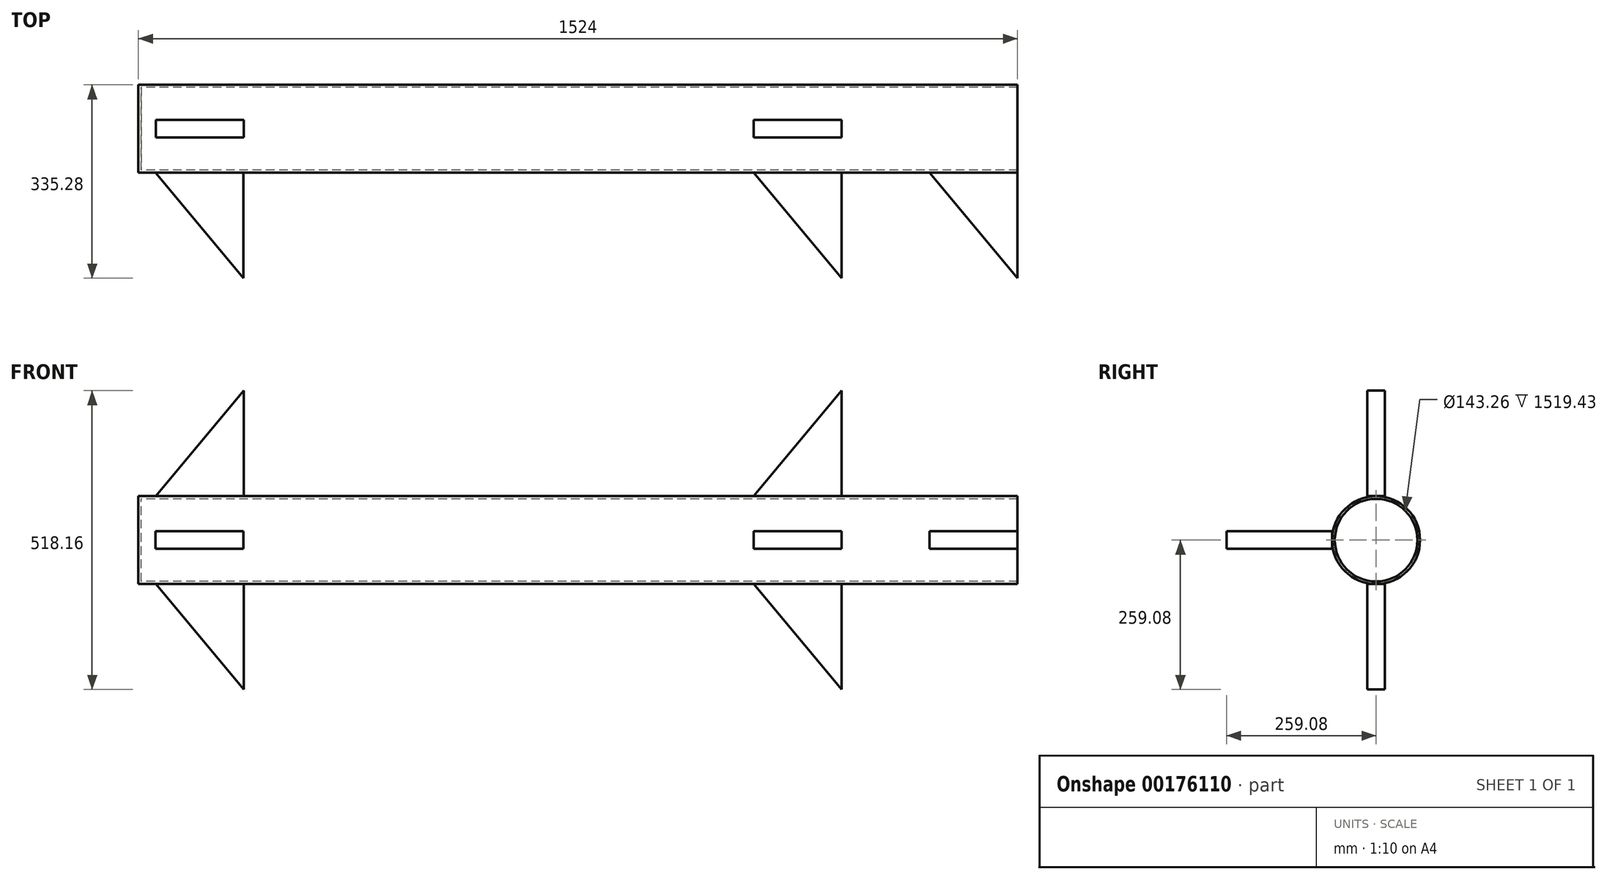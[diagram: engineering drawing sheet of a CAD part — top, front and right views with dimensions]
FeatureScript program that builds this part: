
annotation { "Feature Type Name" : "Feature", "Feature Type Description" : "" }
export const myFeature = defineFeature(function(context is Context, id is Id, definition is map)
    precondition{}
    {
        {
            var Q0;
            Q0=qCreatedBy(makeId("Top.planeOp"),FACE);
            var sketch = newSketch(context, id + "F0", { "sketchPlane" : qUnion([Q0])});
            skLineSegment(sketch, "E0.bottom", {"start": v(762, -76.2) * mm, "end": v(-762, -76.2) * mm});
            skLineSegment(sketch, "E0.top", {"start": v(762, 76.2) * mm, "end": v(-762, 76.2) * mm});
            skLineSegment(sketch, "E0.left", {"start": v(762, -76.2) * mm, "end": v(762, 76.2) * mm});
            skPoint(sketch, "E0.middle", {"position": v(0, 0) * mm});
            skLineSegment(sketch, "E1", {"start": v(-1020.66, 0) * mm, "end": v(-762, -76.2) * mm});
            skLineSegment(sketch, "E2", {"start": v(609.6, 76.2) * mm, "end": v(762, 76.2) * mm});
            skLineSegment(sketch, "E3", {"start": v(762, 76.2) * mm, "end": v(762, 259.08) * mm});
            skLineSegment(sketch, "E4", {"start": v(609.6, 76.2) * mm, "end": v(762, 259.08) * mm});
            skLineSegment(sketch, "E5", {"start": v(762, -76.2) * mm, "end": v(762, -259.08) * mm});
            skLineSegment(sketch, "E6", {"start": v(609.6, -76.2) * mm, "end": v(762, -259.08) * mm});
            skLineSegment(sketch, "E7", {"start": v(-762, 76.2) * mm, "end": v(-732.22, 76.2) * mm});
            skLineSegment(sketch, "E8", {"start": v(-732.22, 76.2) * mm, "end": v(-579.82, 76.2) * mm});
            skLineSegment(sketch, "E9", {"start": v(-579.82, 76.2) * mm, "end": v(-579.82, 259.08) * mm});
            skLineSegment(sketch, "E10", {"start": v(-732.22, 76.2) * mm, "end": v(-579.82, 259.08) * mm});
            skLineSegment(sketch, "E11", {"start": v(-579.82, -76.2) * mm, "end": v(-579.82, -259.08) * mm});
            skLineSegment(sketch, "E12", {"start": v(-732.22, -76.2) * mm, "end": v(-579.82, -259.08) * mm});
            skPoint(sketch, "E13.endSnap0", {"position": v(762, 0) * mm});
            skLineSegment(sketch, "E14", {"start": v(457.2, 76.2) * mm, "end": v(457.2, -76.2) * mm});
            skLineSegment(sketch, "E15", {"start": v(457.2, 76.2) * mm, "end": v(304.8, 76.2) * mm});
            skLineSegment(sketch, "E16", {"start": v(457.2, 76.2) * mm, "end": v(457.2, 259.08) * mm});
            skLineSegment(sketch, "E17", {"start": v(457.2, 0) * mm, "end": v(762, 0) * mm});
            skLineSegment(sketch, "E18", {"start": v(304.8, 76.2) * mm, "end": v(457.2, 259.08) * mm});
            skLineSegment(sketch, "E19", {"start": v(457.2, -76.2) * mm, "end": v(457.2, -259.08) * mm});
            skLineSegment(sketch, "E20", {"start": v(304.8, -76.2) * mm, "end": v(457.2, -259.08) * mm});
            skLineSegment(sketch, "E21", {"start": v(0, 0) * mm, "end": v(-761.8, 0) * mm});
            skLineSegment(sketch, "E22", {"start": v(0, 0) * mm, "end": v(762, 0) * mm});
            skLineSegment(sketch, "E23", {"start": v(-761.8, 0) * mm, "end": v(-1020.66, 0) * mm, "construction": true});
            skLineSegment(sketch, "E24", {"start": v(-761.8, 0) * mm, "end": v(-762, -76.2) * mm});
            skLineSegment(sketch, "E25", {"start": v(-761.8, 0) * mm, "end": v(-762, 76.2) * mm});
            skLineSegment(sketch, "E26", {"start": v(304.8, 76.2) * mm, "end": v(0, 76.2) * mm});
            skSolve(sketch);
        }
        {
            var Q0;
            Q0=qCreatedBy(makeId("Right.planeOp"),FACE);
            var sketch = newSketch(context, id + "F1", { "sketchPlane" : qUnion([Q0])});
            skCircle(sketch, "E27", {"center": v(0, 0) * mm, "radius": 76.2 * mm});
            skSolve(sketch);
        }
        {
            var Q0;
            Q0=makeQuery(id+"F1.imprint","IMPRINT",FACE,{"disambiguationData":[TD([[makeQuery(id+"F1.imprint","IMPRINT",EDGE,{"derivedFrom":sQuery(id+"F1.wireOp",EDGE,"E27")}),1.0]])]});
            extrude(context, id + "F2", {"entities" : qUnion([Q0]), "depth" : 762 * mm, "hasSecondDirection" : true, "secondDirectionOppositeDirection" : true, "secondDirectionDepth" : 762 * mm});
        }
        {
            var Q0;
            Q0=sQuery(id+"F0.wireOp",EDGE,"E24");
            var Q1;
            Q1=sQuery(id+"F0.wireOp",EDGE,"E1");
            var Q2;
            Q2=sQuery(id+"F0.wireOp",EDGE,"E23");
            revolve(context, id + "F3", {"bodyType" : ToolBodyType.SURFACE, "surfaceEntities" : qUnion([Q0, Q1]), "axis" : qUnion([Q2]), "revolveType" : RevolveType.FULL});
        }
        {
            var Q0;
            Q0=makeQuery(id+"F0.imprint","IMPRINT",FACE,{"disambiguationData":[TD([[makeQuery(id+"F0.imprint","IMPRINT",EDGE,{"derivedFrom":sQuery(id+"F0.wireOp",EDGE,"E8")}),1.0]])]});
            var Q1;
            {var subQ0=sQuery(id+"F0.wireOp",EDGE,"E11");Q1=makeQuery(id+"F0.imprint","IMPRINT",FACE,{"disambiguationData":[TD([[makeQuery(id+"F0.imprint","IMPRINT",EDGE,{"derivedFrom":subQ0}),-1.0]])]});}
            var Q2;
            {var subQ0=sQuery(id+"F0.wireOp",EDGE,"E19");Q2=makeQuery(id+"F0.imprint","IMPRINT",FACE,{"disambiguationData":[TD([[makeQuery(id+"F0.imprint","IMPRINT",EDGE,{"derivedFrom":subQ0}),-1.0]])]});}
            var Q3;
            Q3=makeQuery(id+"F0.imprint","IMPRINT",FACE,{"disambiguationData":[TD([[makeQuery(id+"F0.imprint","IMPRINT",EDGE,{"derivedFrom":sQuery(id+"F0.wireOp",EDGE,"E15")}),-1.0]])]});
            var Q4;
            Q4=makeQuery(id+"F0.imprint","IMPRINT",FACE,{"disambiguationData":[TD([[makeQuery(id+"F0.imprint","IMPRINT",EDGE,{"derivedFrom":sQuery(id+"F0.wireOp",EDGE,"E2")}),1.0]])]});
            var Q5;
            {var subQ0=sQuery(id+"F0.wireOp",EDGE,"E5");Q5=makeQuery(id+"F0.imprint","IMPRINT",FACE,{"disambiguationData":[TD([[makeQuery(id+"F0.imprint","IMPRINT",EDGE,{"derivedFrom":subQ0}),-1.0]])]});}
            extrude(context, id + "F4", {"entities" : qUnion([Q0, Q1, Q2, Q3, Q4, Q5]), "operationType" : NewBodyOperationType.ADD, "depth" : 15.24 * mm, "hasSecondDirection" : true, "secondDirectionOppositeDirection" : true, "secondDirectionDepth" : 15.24 * mm});
        }
        {
            var Q0;
            Q0=qCreatedBy(makeId("Front.planeOp"),FACE);
            var sketch = newSketch(context, id + "F5", { "sketchPlane" : qUnion([Q0])});
            skLineSegment(sketch, "E28", {"start": v(0, 0) * mm, "end": v(0, -76.2) * mm});
            skLineSegment(sketch, "E29", {"start": v(0, -76.2) * mm, "end": v(304.8, -76.2) * mm});
            skLineSegment(sketch, "E30", {"start": v(304.8, -76.2) * mm, "end": v(457.2, -76.2) * mm});
            skLineSegment(sketch, "E31", {"start": v(457.2, -76.2) * mm, "end": v(457.2, -259.08) * mm});
            skLineSegment(sketch, "E32", {"start": v(457.2, -259.08) * mm, "end": v(304.8, -76.2) * mm});
            skLineSegment(sketch, "E33", {"start": v(457.2, -76.2) * mm, "end": v(762, -76.2) * mm});
            skLineSegment(sketch, "E34", {"start": v(762, -76.2) * mm, "end": v(609.6, -76.2) * mm});
            skLineSegment(sketch, "E35", {"start": v(762, -76.2) * mm, "end": v(762, -259.08) * mm});
            skLineSegment(sketch, "E36", {"start": v(762, -259.08) * mm, "end": v(609.6, -76.2) * mm});
            skLineSegment(sketch, "E37", {"start": v(0, 0) * mm, "end": v(914.4, 0) * mm, "construction": true});
            skLineSegment(sketch, "E38", {"start": v(0, 0) * mm, "end": v(0, 76.2) * mm});
            skLineSegment(sketch, "E39", {"start": v(0, 76.2) * mm, "end": v(304.8, 76.2) * mm});
            skLineSegment(sketch, "E40", {"start": v(304.8, 76.2) * mm, "end": v(457.2, 76.2) * mm});
            skLineSegment(sketch, "E41", {"start": v(457.2, 76.2) * mm, "end": v(457.2, 259.08) * mm});
            skLineSegment(sketch, "E42", {"start": v(304.8, 76.2) * mm, "end": v(457.2, 259.08) * mm});
            skLineSegment(sketch, "E43", {"start": v(457.2, 76.2) * mm, "end": v(762, 76.2) * mm});
            skLineSegment(sketch, "E44", {"start": v(762, 76.2) * mm, "end": v(609.6, 76.2) * mm});
            skLineSegment(sketch, "E45", {"start": v(762, 76.2) * mm, "end": v(762, 259.08) * mm});
            skLineSegment(sketch, "E46", {"start": v(762, 259.08) * mm, "end": v(609.6, 76.2) * mm});
            skLineSegment(sketch, "E47", {"start": v(0, -76.2) * mm, "end": v(-579.12, -76.2) * mm});
            skLineSegment(sketch, "E48", {"start": v(-579.12, -76.2) * mm, "end": v(-731.52, -76.2) * mm});
            skLineSegment(sketch, "E49", {"start": v(-579.12, -76.2) * mm, "end": v(-579.12, -259.08) * mm});
            skLineSegment(sketch, "E50", {"start": v(-579.12, -259.08) * mm, "end": v(-731.52, -76.2) * mm});
            skLineSegment(sketch, "E51", {"start": v(0, 76.2) * mm, "end": v(-579.12, 76.2) * mm});
            skLineSegment(sketch, "E52", {"start": v(-579.12, 76.2) * mm, "end": v(-579.12, 259.08) * mm});
            skLineSegment(sketch, "E53", {"start": v(-579.12, 76.2) * mm, "end": v(-731.52, 76.2) * mm});
            skLineSegment(sketch, "E54", {"start": v(-731.52, 76.2) * mm, "end": v(-579.12, 259.08) * mm});
            skSolve(sketch);
        }
        {
            var Q0;
            Q0=makeQuery(id+"F5.imprint","IMPRINT",FACE,{"disambiguationData":[TD([[makeQuery(id+"F5.imprint","IMPRINT",EDGE,{"derivedFrom":sQuery(id+"F5.wireOp",EDGE,"E34")}),1.0]])]});
            var Q1;
            Q1=makeQuery(id+"F5.imprint","IMPRINT",FACE,{"disambiguationData":[TD([[makeQuery(id+"F5.imprint","IMPRINT",EDGE,{"derivedFrom":sQuery(id+"F5.wireOp",EDGE,"E44")}),-1.0]])]});
            var Q2;
            Q2=makeQuery(id+"F5.imprint","IMPRINT",FACE,{"disambiguationData":[TD([[makeQuery(id+"F5.imprint","IMPRINT",EDGE,{"derivedFrom":sQuery(id+"F5.wireOp",EDGE,"E30")}),-1.0]])]});
            var Q3;
            Q3=makeQuery(id+"F5.imprint","IMPRINT",FACE,{"disambiguationData":[TD([[makeQuery(id+"F5.imprint","IMPRINT",EDGE,{"derivedFrom":sQuery(id+"F5.wireOp",EDGE,"E40")}),1.0]])]});
            var Q4;
            Q4=makeQuery(id+"F5.imprint","IMPRINT",FACE,{"disambiguationData":[TD([[makeQuery(id+"F5.imprint","IMPRINT",EDGE,{"derivedFrom":sQuery(id+"F5.wireOp",EDGE,"E52")}),1.0]])]});
            var Q5;
            Q5=makeQuery(id+"F5.imprint","IMPRINT",FACE,{"disambiguationData":[TD([[makeQuery(id+"F5.imprint","IMPRINT",EDGE,{"derivedFrom":sQuery(id+"F5.wireOp",EDGE,"E48")}),1.0]])]});
            extrude(context, id + "F6", {"entities" : qUnion([Q0, Q1, Q2, Q3, Q4, Q5]), "operationType" : NewBodyOperationType.ADD, "depth" : 15.24 * mm, "hasSecondDirection" : true, "secondDirectionOppositeDirection" : true, "secondDirectionDepth" : 15.24 * mm});
        }
        {
            var Q0;
            Q0=makeQuery(id+"F2.opExtrude","CAP_FACE",FACE,{"disambiguationData":[OSD([sQuery(id+"F1.wireOp",EDGE,"E27")])],"isStart":false});
            shell(context, id + "F7", {"entities" : qUnion([Q0]), "thickness" : 4.57 * mm});
        }
    });
